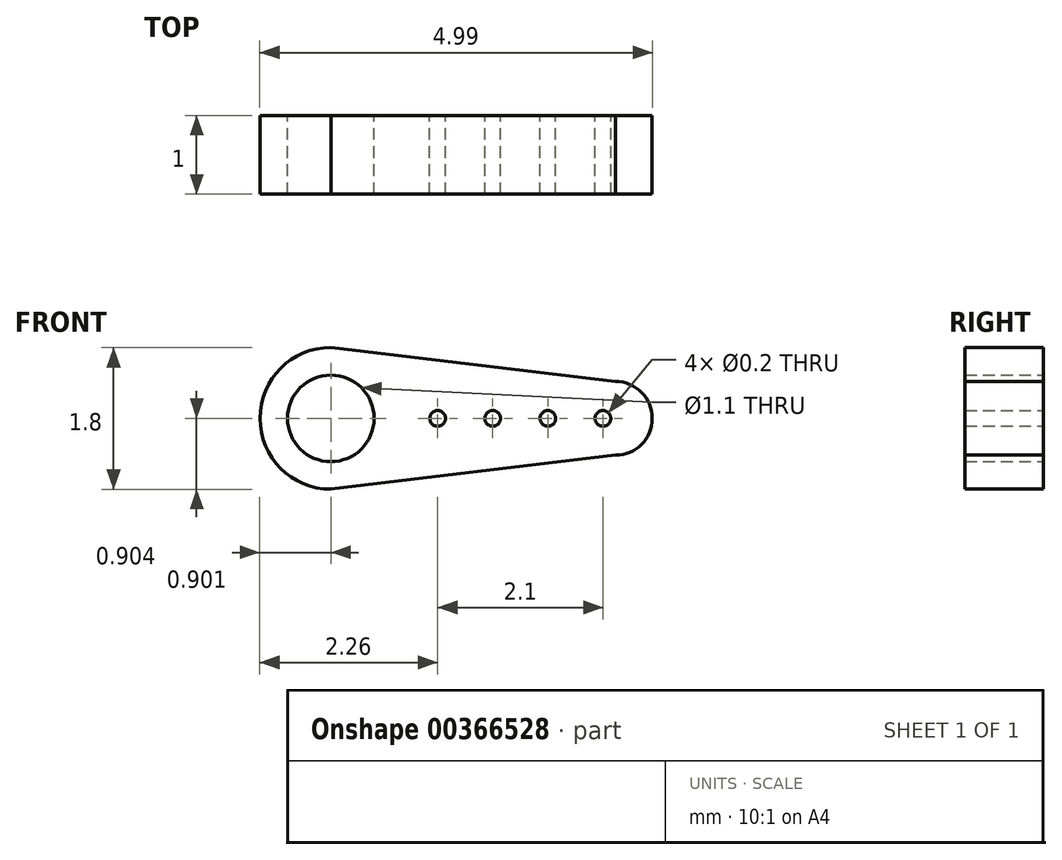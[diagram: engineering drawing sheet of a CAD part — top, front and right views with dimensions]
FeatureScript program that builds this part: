
annotation { "Feature Type Name" : "Feature", "Feature Type Description" : "" }
export const myFeature = defineFeature(function(context is Context, id is Id, definition is map)
    precondition{}
    {
        {
            var Q0;
            Q0=qCreatedBy(makeId("Front.planeOp"),FACE);
            var sketch = newSketch(context, id + "F0", { "sketchPlane" : qUnion([Q0])});
            skArc(sketch, "E0", {"start": v(-23.57, 25.5) * mm, "mid": v(-24.47, 24.6) * mm, "end": v(-23.57, 23.7) * mm});
            skCircle(sketch, "E1", {"center": v(-23.57, 24.6) * mm, "radius": 0.55 * mm});
            skArc(sketch, "E2", {"start": v(-19.95, 24.12) * mm, "mid": v(-19.48, 24.6) * mm, "end": v(-19.95, 25.06) * mm});
            skLineSegment(sketch, "E3", {"start": v(-23.57, 25.5) * mm, "end": v(-19.95, 25.06) * mm});
            skLineSegment(sketch, "E4", {"start": v(-19.95, 24.12) * mm, "end": v(-23.57, 23.7) * mm});
            skLineSegment(sketch, "E5", {"start": v(-23.57, 24.6) * mm, "end": v(-19.95, 24.6) * mm});
            skCircle(sketch, "E6", {"center": v(-22.21, 24.6) * mm, "radius": 0.1 * mm});
            skCircle(sketch, "E7.1.0.0", {"center": v(-21.51, 24.6) * mm, "radius": 0.1 * mm});
            skCircle(sketch, "E7.2.0.0", {"center": v(-20.81, 24.6) * mm, "radius": 0.1 * mm});
            skCircle(sketch, "E7.3.0.0", {"center": v(-20.11, 24.6) * mm, "radius": 0.1 * mm});
            skLineSegment(sketch, "E7.direction1", {"start": v(-22.21, 24.6) * mm, "end": v(-21.51, 24.6) * mm, "construction": true});
            skSolve(sketch);
        }
        {
            var Q0;
            Q0=makeQuery(id+"F0.imprint","IMPRINT",FACE,{"disambiguationData":[TD([[makeQuery(id+"F0.imprint","IMPRINT",EDGE,{"derivedFrom":sQuery(id+"F0.wireOp",EDGE,"E0")}),1.0]])]});
            extrude(context, id + "F1", {"entities" : qUnion([Q0]), "depth" : 1 * mm});
        }
    });
